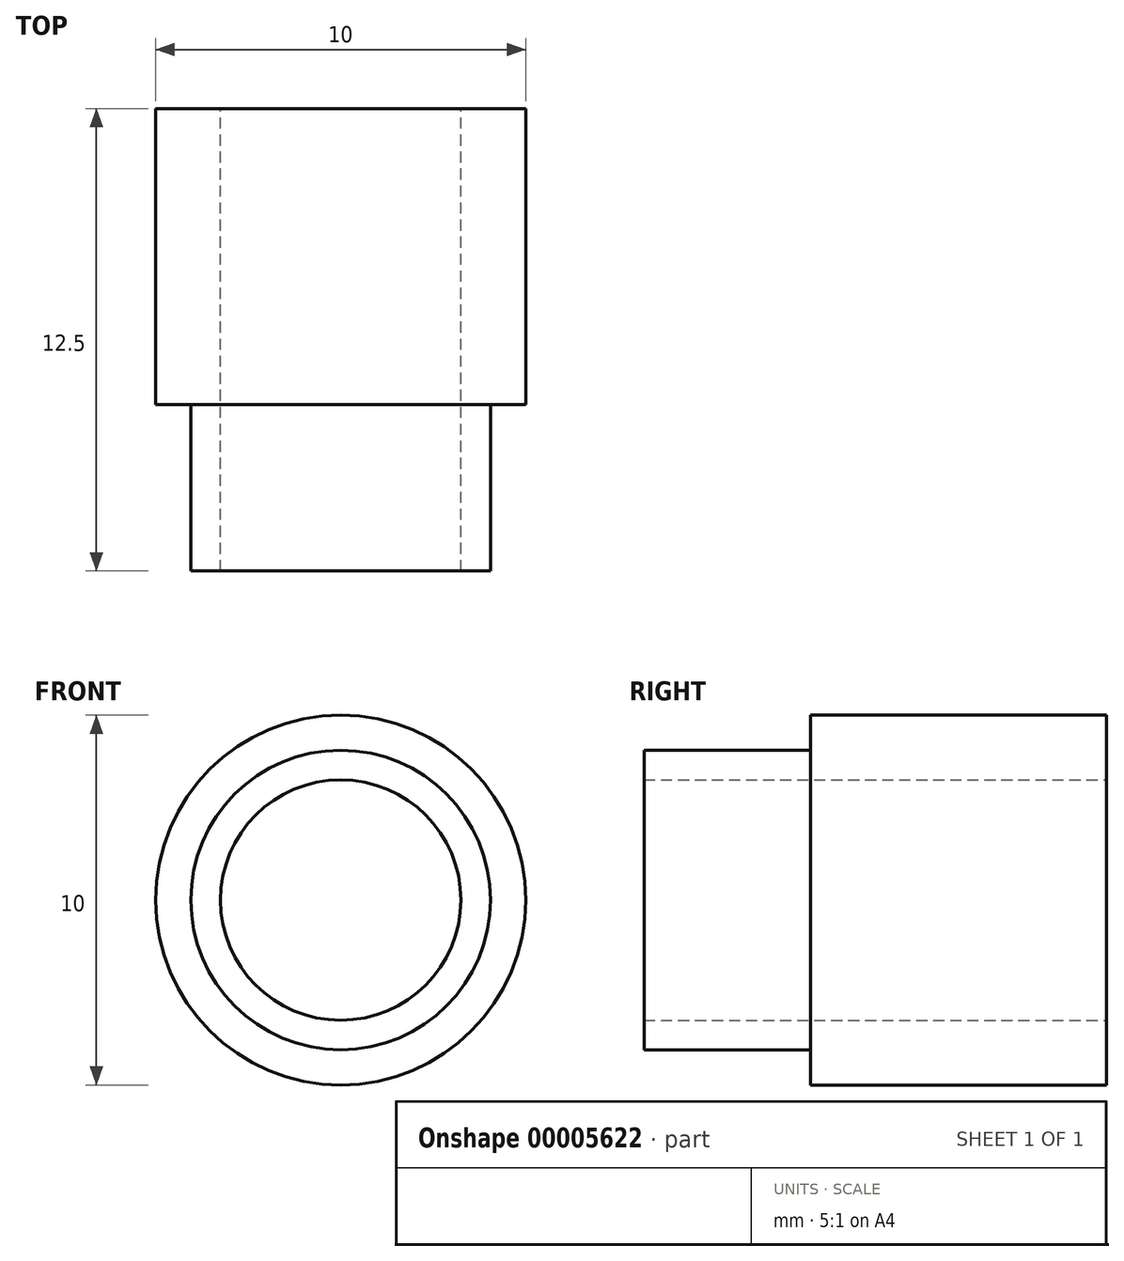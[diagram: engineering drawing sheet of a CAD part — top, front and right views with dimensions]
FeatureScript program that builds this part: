
annotation { "Feature Type Name" : "Feature", "Feature Type Description" : "" }
export const myFeature = defineFeature(function(context is Context, id is Id, definition is map)
    precondition{}
    {
        {
            var Q0;
            Q0=qCreatedBy(makeId("Front.planeOp"),FACE);
            var sketch = newSketch(context, id + "F0", { "sketchPlane" : qUnion([Q0])});
            skCircle(sketch, "E0", {"center": v(0, 0) * mm, "radius": 3.25 * mm});
            skCircle(sketch, "E1", {"center": v(0, 0) * mm, "radius": 4.05 * mm});
            skCircle(sketch, "E2", {"center": v(0, 0) * mm, "radius": 5 * mm});
            skLineSegment(sketch, "E3", {"start": v(9.46, 7.46) * mm, "end": v(9.46, -5.8) * mm, "construction": true});
            skCircle(sketch, "E4.0.MirrorC", {"center": v(18.93, 0) * mm, "radius": 3.25 * mm});
            skCircle(sketch, "E4.1.MirrorC", {"center": v(18.93, 0) * mm, "radius": 5 * mm});
            skCircle(sketch, "E4.2.MirrorC", {"center": v(18.93, 0) * mm, "radius": 4.05 * mm});
            skLineSegment(sketch, "E5", {"start": v(-8.84, 7.46) * mm, "end": v(-8.84, -6.44) * mm, "construction": true});
            skCircle(sketch, "E6.0.MirrorC", {"center": v(-17.69, 0) * mm, "radius": 5 * mm});
            skCircle(sketch, "E6.1.MirrorC", {"center": v(-17.69, 0) * mm, "radius": 4.05 * mm});
            skCircle(sketch, "E6.2.MirrorC", {"center": v(-17.69, 0) * mm, "radius": 3.25 * mm});
            skSolve(sketch);
        }
        {
            var Q0;
            Q0=makeQuery(id+"F0.imprint","IMPRINT",FACE,{"disambiguationData":[TD([[makeQuery(id+"F0.imprint","IMPRINT",EDGE,{"derivedFrom":sQuery(id+"F0.wireOp",EDGE,"E0")}),-1.0]])]});
            extrude(context, id + "F1", {"entities" : qUnion([Q0]), "depth" : (((65 + 15) - 55) / 2) * mm});
        }
        {
            var Q0;
            Q0=makeQuery(id+"F0.imprint","IMPRINT",FACE,{"disambiguationData":[TD([[makeQuery(id+"F0.imprint","IMPRINT",EDGE,{"derivedFrom":sQuery(id+"F0.wireOp",EDGE,"E1")}),-1.0]])]});
            extrude(context, id + "F2", {"entities" : qUnion([Q0]), "operationType" : NewBodyOperationType.ADD, "depth" : (((65 + 6) - 55) / 2) * mm});
        }
    });
